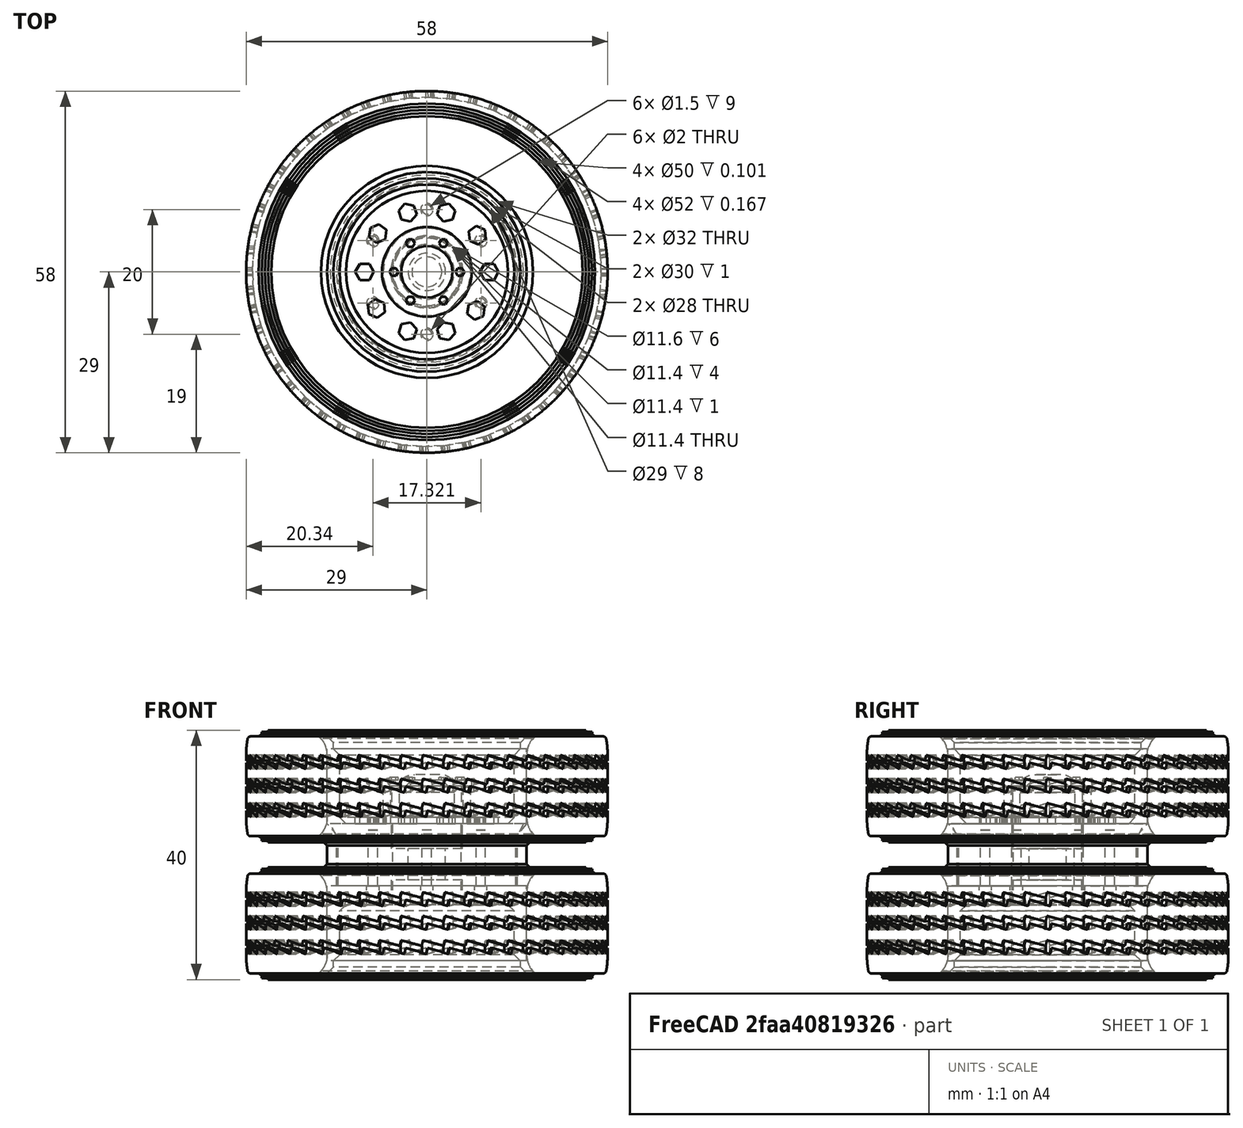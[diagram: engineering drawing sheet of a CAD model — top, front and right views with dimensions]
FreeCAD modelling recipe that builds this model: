
FCSTD DOCUMENT  (FreeCAD 0.18.4R)
Label: wheels
License: All rights reserved
LicenseURL: http://en.wikipedia.org/wiki/All_rights_reserved
objects: Part::Cylinder×44, Part::Cut×27, Part::MultiFuse×25, Part::Feature×24, Part::Fillet×10, Part::Chamfer×10, Part::RegularPolygon×4, Part::Extrusion×4, Part::Box×2, Part::Mirroring×2
note: 152 computed .brp shape members not serialized (recipe doc carries the construction recipe); baked Part::Feature solids carry a one-line shape summary decoded from their .brp

FEATURE [Part::Cylinder] Cylinder
  Angle = 360
  AttacherType = Attacher::AttachEngine3D
  Height = 18
  Radius = 29
FEATURE [Part::Cylinder] Cylinder001
  Angle = 360
  AttacherType = Attacher::AttachEngine3D
  Height = 18
  Radius = 16
FEATURE [Part::Cut] Cut
  Base = -> Cylinder
  Refine = true
  Tool = -> Cylinder001
FEATURE [Part::Fillet] Fillet
  Base = -> Cut
  Edges = 2 edges r=4: [Edge4,Edge5]
FEATURE [Part::Cylinder] Cylinder002
  Angle = 360
  AttacherType = Attacher::AttachEngine3D
  Height = 16
  Placement = pos=(0,0,1) rot=(0,0,1;0rad)
  Radius = 29
FEATURE [Part::Cylinder] Cylinder003
  Angle = 360
  AttacherType = Attacher::AttachEngine3D
  Height = 18
  Radius = 21
FEATURE [Part::Cut] Cut001
  Base = -> Cylinder002
  Refine = true
  Tool = -> Cylinder003
FEATURE [Part::Fillet] Fillet001
  Base = -> Fillet
  Edges = 2 edges r=5: [Edge2,Edge6]
FEATURE [Part::Box] Box  label="Cube"
  AttacherType = Attacher::AttachEngine3D
  Height = 2
  Length = 3
  Placement = pos=(27,0,4) rot=(0,0,1;0.05236rad)
  Width = 4
FEATURE [Part::Box] Box001  label="Cube001"
  AttacherType = Attacher::AttachEngine3D
  Height = 2
  Length = 2
  Placement = pos=(28,-1,5) rot=(0,0,1;0.05236rad)
  Width = 4
FEATURE [Part::Cut] Cut002
  Base = -> Box001
  Placement = pos=(0,-1,0) rot=(-1,0,0;0.261799rad)
  Refine = true
  Tool = -> Box
FEATURE [Part::Feature] Cut002001  label="Cut003"
  Placement = pos=(0,-1,0) rot=(-1,0,0;0.261799rad)
  shape: bbox 2.207 x 4.477 x 2.231 mm, 8 faces (baked)
FEATURE [Part::Mirroring] Part__Mirroring  label="Cut003 (Mirror #1)"
  Base = (0,0,0)
  Normal = (1,0,0)
  Source = -> Cut002001
FEATURE [Part::Mirroring] Part__Mirroring001  label="Cut003 (Mirror #2)"
  Base = (0,0,0)
  Normal = (0,1,0)
  Source = -> Part__Mirroring
FEATURE [Part::MultiFuse] Fusion001
  Refine = true
  Shapes = -> [Part__Mirroring001,Cut002]
FEATURE [Part::Feature] Fusion001001  label="Fusion002"
  Placement = pos=(0,0,0) rot=(0,0,1;3.01942rad)
  shape: bbox 60.06 x 8.444 x 2.231 mm, 16 faces, 2 solids (baked)
FEATURE [Part::Feature] Fusion001002  label="Fusion003"
  Placement = pos=(0,0,0) rot=(0,0,1;2.89725rad)
  shape: bbox 59.65 x 15.62 x 2.231 mm, 16 faces, 2 solids (baked)
FEATURE [Part::Feature] Fusion001003  label="Fusion004"
  Placement = pos=(0,0,0) rot=(0,0,1;2.77507rad)
  shape: bbox 58.35 x 22.57 x 2.231 mm, 16 faces, 2 solids (baked)
FEATURE [Part::Feature] Fusion001004  label="Fusion005"
  Placement = pos=(0,0,0) rot=(0,0,1;2.6529rad)
  shape: bbox 56.18 x 29.17 x 2.231 mm, 16 faces, 2 solids (baked)
FEATURE [Part::MultiFuse] Fusion001005
  Refine = true
  Shapes = -> [Fusion001001,Fusion001004,Fusion001002,Fusion001003]
FEATURE [Part::Feature] Fusion001005001  label="Fusion001006"
  Placement = pos=(0,0,0) rot=(0,0,-1;0.488692rad)
  shape: bbox 53.17 x 50.38 x 2.231 mm, 76 faces, 2 solids (baked)
FEATURE [Part::MultiFuse] Fusion001005002
  Refine = true
  Shapes = -> [Fusion001005001,Fusion001005]
FEATURE [Part::Feature] Fusion001005002001  label="Fusion001005003"
  Placement = pos=(0,0,0) rot=(0,0,-1;0.977384rad)
  shape: bbox 33.83 x 60.06 x 2.231 mm, 156 faces, 2 solids (baked)
FEATURE [Part::Feature] Fusion001005002002  label="Fusion001005004"
  Placement = pos=(0,0,0) rot=(0,0,-1;1.95477rad)
  shape: bbox 58.92 x 55.8 x 2.231 mm, 156 faces, 2 solids (baked)
FEATURE [Part::Feature] Fusion001005002003  label="Fusion001005005"
  Placement = pos=(0,0,0) rot=(0,0,1;0.10472rad)
  shape: bbox 59.79 x 13.8 x 2.231 mm, 16 faces, 2 solids (baked)
FEATURE [Part::MultiFuse] Fusion001005002004
  Placement = pos=(0,0,3.2) rot=(0,0,1;0rad)
  Refine = true
  Shapes = -> [Fusion001,Fusion001005002001,Fusion001005002003,Fusion001005002002,Fusion001005002]
FEATURE [Part::Feature] Fusion001005002004001  label="Fusion001005002005"
  Placement = pos=(0,0,7) rot=(0,0,1;0rad)
  shape: bbox 60.06 x 60.06 x 2.231 mm, 536 faces (baked)
FEATURE [Part::Feature] Fusion001005002004002  label="Fusion001005002006"
  Placement = pos=(0,0,-0.7) rot=(0,0,1;0rad)
  shape: bbox 60.06 x 60.06 x 2.231 mm, 536 faces (baked)
FEATURE [Part::MultiFuse] Fusion001005002004003
  Refine = true
  Shapes = -> [Fusion001005002004002,Fusion001005002004001,Fusion001005002004]
FEATURE [Part::Cylinder] Cylinder004
  Angle = 360
  AttacherType = Attacher::AttachEngine3D
  Height = 40
  Placement = pos=(0,0,-11) rot=(0,0,1;0rad)
  Radius = 29
FEATURE [Part::Fillet] Fillet002
  Base = -> Cylinder004
  Edges = 2 edges r=15: [Edge1,Edge3]
FEATURE [Part::Cylinder] Cylinder005
  Angle = 360
  AttacherType = Attacher::AttachEngine3D
  Height = 40
  Placement = pos=(0,0,-11) rot=(0,0,1;0rad)
  Radius = 30
FEATURE [Part::Cut] Cut002002
  Base = -> Cylinder005
  Refine = true
  Tool = -> Fillet002
FEATURE [Part::Cut] Cut002003
  Base = -> Cut001
  Refine = true
  Tool = -> Cut002002
FEATURE [Part::Fillet] Fillet003
  Base = -> Cut002003
  Edges = 2 edges r=0.5: [Edge5,Edge7]
FEATURE [Part::MultiFuse] Fusion
  Refine = true
  Shapes = -> [Fillet001,Fillet003]
FEATURE [Part::Cut] Cut002004
  Base = -> Fusion
  Refine = true
  Tool = -> Fusion001005002004003
FEATURE [Part::Cylinder] Cylinder006
  Angle = 360
  AttacherType = Attacher::AttachEngine3D
  Height = 17.5
  Placement = pos=(0,0,0.25) rot=(0,0,1;0rad)
  Radius = 26.5
FEATURE [Part::Cylinder] Cylinder007
  Angle = 360
  AttacherType = Attacher::AttachEngine3D
  Height = 17.5
  Placement = pos=(0,0,0.25) rot=(0,0,1;0rad)
  Radius = 26
FEATURE [Part::Cut] Cut002005
  Base = -> Cylinder006
  Refine = true
  Tool = -> Cylinder007
FEATURE [Part::Cylinder] Cylinder008
  Angle = 360
  AttacherType = Attacher::AttachEngine3D
  Height = 18
  Radius = 25.5
FEATURE [Part::Cylinder] Cylinder009
  Angle = 360
  AttacherType = Attacher::AttachEngine3D
  Height = 18
  Radius = 25
FEATURE [Part::Cut] Cut002006
  Base = -> Cylinder008
  Refine = true
  Tool = -> Cylinder009
FEATURE [Part::MultiFuse] Fusion001005002004004  label="tire-inner"
  Refine = true
  Shapes = -> [Cut002004,Cut002005,Cut002006]
FEATURE [Part::Cylinder] Cylinder719
  Angle = 360
  AttacherType = Attacher::AttachEngine3D
  Height = 14
  Radius = 16
FEATURE [Part::Cylinder] Cylinder720
  Angle = 360
  AttacherType = Attacher::AttachEngine3D
  Height = 2
  Radius = 17
FEATURE [Part::MultiFuse] Fusion088026026
  Placement = pos=(0,0,1) rot=(0,0,1;0rad)
  Refine = true
  Shapes = -> [Cylinder719,Cylinder720]
FEATURE [Part::Cylinder] Cylinder793
  Angle = 360
  AttacherType = Attacher::AttachEngine3D
  Height = 18
  Radius = 29
FEATURE [Part::Cylinder] Cylinder794
  Angle = 360
  AttacherType = Attacher::AttachEngine3D
  Height = 18
  Radius = 16
FEATURE [Part::Cut] Cut176013009049
  Base = -> Cylinder793
  Refine = true
  Tool = -> Cylinder794
FEATURE [Part::Fillet] Fillet567
  Base = -> Cut176013009049
  Edges = 2 edges r=4: [Edge4,Edge5]
FEATURE [Part::Fillet] Fillet566
  Base = -> Fillet567
  Edges = 2 edges r=5: [Edge2,Edge6]
FEATURE [Part::Cut] Cut176013009050
  Base = -> Fusion088026026
  Refine = true
  Tool = -> Fillet566
FEATURE [Part::Feature] Fusion001005002004004001  label="tire-outer"
  Placement = pos=(0,0,22) rot=(0,0,1;0rad)
  shape: bbox 59.64 x 59.64 x 18 mm, 1212 faces (baked)
FEATURE [Part::Cylinder] Cylinder795
  Angle = 360
  AttacherType = Attacher::AttachEngine3D
  Height = 2
  Placement = pos=(0,0,37) rot=(-1,0,0;0rad)
  Radius = 17
FEATURE [Part::Cylinder] Cylinder796
  Angle = 360
  AttacherType = Attacher::AttachEngine3D
  Height = 24
  Placement = pos=(0,0,15) rot=(-1,0,0;0rad)
  Radius = 16
FEATURE [Part::MultiFuse] Fusion001005002004004002
  Refine = true
  Shapes = -> [Cylinder796,Cylinder795]
FEATURE [Part::Cylinder] Cylinder797
  Angle = 360
  AttacherType = Attacher::AttachEngine3D
  Height = 18
  Radius = 16
FEATURE [Part::Cylinder] Cylinder798
  Angle = 360
  AttacherType = Attacher::AttachEngine3D
  Height = 18
  Radius = 29
FEATURE [Part::Cut] Cut176013009051
  Base = -> Cylinder798
  Refine = true
  Tool = -> Cylinder797
FEATURE [Part::Fillet] Fillet569
  Base = -> Cut176013009051
  Edges = 2 edges r=4: [Edge4,Edge5]
FEATURE [Part::Fillet] Fillet568
  Base = -> Fillet569
  Edges = 2 edges r=5: [Edge2,Edge6]
  Placement = pos=(0,0,22) rot=(0,0,1;0rad)
FEATURE [Part::Cut] Cut176013009052
  Base = -> Fusion001005002004004002
  Refine = true
  Tool = -> Fillet568
FEATURE [Part::Cylinder] Cylinder799
  Angle = 360
  AttacherType = Attacher::AttachEngine3D
  Height = 10
  Placement = pos=(0,0,15) rot=(-1,0,0;0rad)
  Radius = 17
FEATURE [Part::Feature] Fillet568001  label="Fillet570"
  Placement = pos=(0,0,22) rot=(0,0,1;0rad)
  shape: bbox 62.78 x 62.78 x 18 mm, 8 faces (baked)
FEATURE [Part::Feature] Fillet566001  label="Fillet571"
  shape: bbox 62.78 x 62.78 x 18 mm, 8 faces (baked)
FEATURE [Part::MultiFuse] Fusion001005002004004003
  Refine = true
  Shapes = -> [Fillet568001,Fillet566001]
FEATURE [Part::Cut] Cut176013009053
  Base = -> Cylinder799
  Refine = true
  Tool = -> Fusion001005002004004003
FEATURE [Part::Cylinder] Cylinder800
  Angle = 360
  AttacherType = Attacher::AttachEngine3D
  Height = 10
  Radius = 14.25
FEATURE [Part::Cylinder] Cylinder801
  Angle = 360
  AttacherType = Attacher::AttachEngine3D
  Height = 10
  Radius = 16
FEATURE [Part::Cut] Cut176013009054
  Base = -> Cylinder801
  Placement = pos=(0,0,15) rot=(0,0,1;0rad)
  Refine = true
  Tool = -> Cylinder800
FEATURE [Part::Cylinder] Cylinder802
  Angle = 360
  AttacherType = Attacher::AttachEngine3D
  Height = 10
  Placement = pos=(0,0,15) rot=(-1,0,0;0rad)
  Radius = 14.5
FEATURE [Part::Cut] Cut176013009055
  Base = -> Cut176013009053
  Refine = true
  Tool = -> Cylinder802
FEATURE [Part::Cylinder] Cylinder803
  Angle = 360
  AttacherType = Attacher::AttachEngine3D
  Height = 5
  Placement = pos=(0,0,17.5) rot=(-1,0,0;0rad)
  Radius = 17
FEATURE [Part::Cylinder] Cylinder804
  Angle = 360
  AttacherType = Attacher::AttachEngine3D
  Height = 5
  Placement = pos=(0,0,17.5) rot=(-1,0,0;0rad)
  Radius = 16
FEATURE [Part::Cut] Cut176013009058
  Base = -> Cylinder803
  Refine = true
  Tool = -> Cylinder804
FEATURE [Part::Chamfer] Chamfer017002
  Base = -> Cut176013009058
  Edges = 2 edges r=0.999: [Edge4,Edge5]
FEATURE [Part::Cylinder] Cylinder805
  Angle = 360
  AttacherType = Attacher::AttachEngine3D
  Height = 12
  Radius = 14
FEATURE [Part::Cut] Cut176013009060
  Base = -> Cut176013009050
  Refine = true
  Tool = -> Cylinder805
FEATURE [Part::Cylinder] Cylinder806
  Angle = 360
  AttacherType = Attacher::AttachEngine3D
  Height = 3
  Radius = 15
FEATURE [Part::Cut] Cut176013009061
  Base = -> Cut176013009060
  Refine = true
  Tool = -> Cylinder806
FEATURE [Part::Chamfer] Chamfer017003
  Base = -> Cut176013009061
  Edges = 1 edges r=1: [Edge9]
FEATURE [Part::Chamfer] Chamfer017004
  Base = -> Chamfer017003
  Edges = 1 edges r=0.999: [Edge11]
FEATURE [Part::Chamfer] Chamfer017005
  Base = -> Chamfer017004
  Edges = 1 edges r=1: [Edge8]
FEATURE [Part::Chamfer] Chamfer017006
  Base = -> Cut176013009054
  Edges = 1 edges: [Edge4 r1=1.749 r2=2]
FEATURE [Part::Cut] Cut176013009062
  Base = -> Cut176013009052
  Refine = true
  Tool = -> Chamfer017006
FEATURE [Part::Chamfer] Chamfer017007
  Base = -> Cut176013009055
  Edges = 1 edges: [Edge8 r1=1 r2=2]
FEATURE [Part::Cut] Cut176013009063  label="rim-central"
  Base = -> Chamfer017007
  Refine = true
  Tool = -> Chamfer017002
FEATURE [Part::Cylinder] Cylinder807
  Angle = 360
  AttacherType = Attacher::AttachEngine3D
  Height = 15
  Placement = pos=(0,0,25) rot=(-1,0,0;0rad)
  Radius = 14
FEATURE [Part::Cylinder] Cylinder808
  Angle = 360
  AttacherType = Attacher::AttachEngine3D
  Height = 3
  Placement = pos=(0,0,37) rot=(-1,0,0;0rad)
  Radius = 15
FEATURE [Part::MultiFuse] Fusion001005002004004004
  Refine = true
  Shapes = -> [Cylinder807,Cylinder808]
FEATURE [Part::Cut] Cut176013009064
  Base = -> Cut176013009062
  Refine = true
  Tool = -> Fusion001005002004004004
FEATURE [Part::Chamfer] Chamfer017008
  Base = -> Cut176013009064
  Edges = 2 edges r=1: [Edge14,Edge19]
FEATURE [Part::Chamfer] Chamfer017009
  Base = -> Chamfer017008
  Edges = 1 edges r=0.999: [Edge11]
FEATURE [Part::Cylinder] Cylinder809
  Angle = 360
  AttacherType = Attacher::AttachEngine3D
  Height = 40
  Radius = 3
FEATURE [Part::Cylinder] Cylinder810
  Angle = 360
  AttacherType = Attacher::AttachEngine3D
  Height = 4
  Placement = pos=(0,0,21) rot=(-1,0,0;0rad)
  Radius = 5.7
FEATURE [Part::Cylinder] Cylinder811
  Angle = 360
  AttacherType = Attacher::AttachEngine3D
  Height = 4
  Placement = pos=(0,0,12) rot=(-1,0,0;0rad)
  Radius = 5.7
FEATURE [Part::MultiFuse] Fusion001005002004004005
  Refine = true
  Shapes = -> [Cylinder809,Cylinder810,Cylinder811]
FEATURE [Part::Cut] Cut176013009065
  Base = -> Chamfer017005
  Refine = true
  Tool = -> Fusion001005002004004005
FEATURE [Part::RegularPolygon] RegularPolygon  label="Regular polygon"
  AttacherType = Attacher::AttachEngine3D
  Circumradius = 1.5
  Placement = pos=(-10,0,0) rot=(0,0,1;0rad)
  Polygon = 6
FEATURE [Part::Extrusion] Extrude
  Base = -> RegularPolygon
  Dir = (0,0,1)
  DirMode = 0
  FaceMakerClass = Part::FaceMakerBullseye
  LengthFwd = 1
  LengthRev = 0
  Placement = pos=(0,0,11) rot=(0,0,1;0rad)
  Solid = true
  Symmetric = false
FEATURE [Part::RegularPolygon] RegularPolygon001  label="Regular polygon001"
  AttacherType = Attacher::AttachEngine3D
  Circumradius = 1.5
  Placement = pos=(-10,0,0) rot=(0,0,1;0rad)
  Polygon = 6
FEATURE [Part::Extrusion] Extrude001
  Base = -> RegularPolygon001
  Dir = (0,0,1)
  DirMode = 0
  FaceMakerClass = Part::FaceMakerBullseye
  LengthFwd = 1
  LengthRev = 0
  Placement = pos=(20,0,11) rot=(0,0,1;0rad)
  Solid = true
  Symmetric = false
FEATURE [Part::MultiFuse] Fusion001005002004004005002
  Refine = true
  Shapes = -> [Extrude001,Extrude]
FEATURE [Part::Feature] Fusion001005002004004005002001  label="Fusion001005002004004005003"
  Placement = pos=(0,0,0) rot=(0,0,1;0.628319rad)
  shape: bbox 18.92 x 14.74 x 1 mm, 16 faces, 2 solids (baked)
FEATURE [Part::Feature] Fusion001005002004004005002002  label="Fusion001005002004004005004"
  Placement = pos=(0,0,0) rot=(0,0,1;1.25664rad)
  shape: bbox 9.115 x 21.87 x 1 mm, 16 faces, 2 solids (baked)
FEATURE [Part::Feature] Fusion001005002004004005002003  label="Fusion001005002004004005005"
  Placement = pos=(0,0,0) rot=(0,0,1;1.88496rad)
  shape: bbox 9.115 x 21.87 x 1 mm, 16 faces, 2 solids (baked)
FEATURE [Part::Feature] Fusion001005002004004005002004  label="Fusion001005002004004005006"
  Placement = pos=(0,0,0) rot=(0,0,1;2.47837rad)
  shape: bbox 18.54 x 15.28 x 1 mm, 16 faces, 2 solids (baked)
FEATURE [Part::MultiFuse] Fusion001005002004004005002005
  Placement = pos=(0,0,14) rot=(0,0,1;0rad)
  Refine = true
  Shapes = -> [Fusion001005002004004005002,Fusion001005002004004005002001,Fusion001005002004004005002002,Fusion001005002004004005002004,Fusion001005002004004005002003]
FEATURE [Part::Cylinder] Cylinder812
  Angle = 360
  AttacherType = Attacher::AttachEngine3D
  Height = 6
  Placement = pos=(0,0,25) rot=(-1,0,0;0rad)
  Radius = 7
FEATURE [Part::Cylinder] Cylinder813
  Angle = 360
  AttacherType = Attacher::AttachEngine3D
  Height = 6
  Placement = pos=(0,0,25) rot=(-1,0,0;0rad)
  Radius = 5.8
FEATURE [Part::Cut] Cut176013009067
  Base = -> Cylinder812
  Refine = true
  Tool = -> Cylinder813
FEATURE [Part::Feature] Fusion058011001  label="Fusion058012"
  Placement = pos=(0,0,0) rot=(0,0,1;1.0472rad)
  shape: bbox 6.7 x 10.39 x 0.5 mm, 16 faces, 2 solids (baked)
FEATURE [Part::Cylinder] Cylinder100
  Angle = 360
  AttacherType = Attacher::AttachEngine3D
  Height = 5
  Placement = pos=(0,0,11) rot=(0,0,1;0rad)
  Radius = 6
FEATURE [Part::Cylinder] Cylinder098
  Angle = 360
  AttacherType = Attacher::AttachEngine3D
  Height = 11
  Placement = pos=(0,0,12) rot=(0,0,1;0rad)
  Radius = 4.4
FEATURE [Part::Cylinder] Cylinder099
  Angle = 360
  AttacherType = Attacher::AttachEngine3D
  Height = 1
  Placement = pos=(0,0,20) rot=(0,0,1;0rad)
  Radius = 7.2
FEATURE [Part::Feature] Fusion058011002  label="Fusion058013"
  Placement = pos=(0,0,0) rot=(0,0,1;2.0944rad)
  shape: bbox 6.7 x 10.39 x 0.5 mm, 16 faces, 2 solids (baked)
FEATURE [Part::Fillet] Fillet059
  Base = -> Cylinder099
  Edges = 1 edges r=0.5: [Edge1]
  Placement = pos=(0,0,11) rot=(0,0,1;0rad)
FEATURE [Part::RegularPolygon] RegularPolygon003  label="Regular polygon003"
  AttacherType = Attacher::AttachEngine3D
  Circumradius = 0.7
  Polygon = 6
FEATURE [Part::Extrusion] Extrude010003
  Base = -> RegularPolygon003
  Dir = (0,0,1)
  DirMode = 0
  FaceMakerClass = Part::FaceMakerBullseye
  LengthFwd = 0.5
  LengthRev = 0
  Placement = pos=(-5.3,0,21.9) rot=(0,0,1;0rad)
  Solid = true
  Symmetric = false
FEATURE [Part::Cylinder] Cylinder101
  Angle = 360
  AttacherType = Attacher::AttachEngine3D
  Height = 3.8
  Placement = pos=(0,0,19.4) rot=(0,0,1;0rad)
  Radius = 5
FEATURE [Part::Fillet] Fillet006004006
  Base = -> Cylinder101
  Edges = 1 edges r=3: [Edge1]
  Placement = pos=(0,0,9.7) rot=(0,0,1;0rad)
FEATURE [Part::MultiFuse] Fusion041
  Refine = true
  Shapes = -> [Cylinder098,Cylinder100]
FEATURE [Part::Chamfer] Chamfer001
  Base = -> Fusion041
  Edges = 1 edges r=2: [Edge1]
  Placement = pos=(0,0,9) rot=(0,0,1;0rad)
FEATURE [Part::Cylinder] Cylinder097
  Angle = 360
  AttacherType = Attacher::AttachEngine3D
  Height = 6
  Placement = pos=(0,0,26) rot=(0,0,1;0rad)
  Radius = 5.55
FEATURE [Part::RegularPolygon] RegularPolygon002  label="Regular polygon002"
  AttacherType = Attacher::AttachEngine3D
  Circumradius = 0.7
  Polygon = 6
FEATURE [Part::Extrusion] Extrude010002
  Base = -> RegularPolygon002
  Dir = (0,0,1)
  DirMode = 0
  FaceMakerClass = Part::FaceMakerBullseye
  LengthFwd = 0.5
  LengthRev = 0
  Placement = pos=(5.3,0,21.9) rot=(0,0,1;0rad)
  Solid = true
  Symmetric = false
FEATURE [Part::MultiFuse] Fusion058011
  Refine = true
  Shapes = -> [Extrude010003,Extrude010002]
FEATURE [Part::MultiFuse] Fusion058011003
  Placement = pos=(0,0,10) rot=(0,0,1;0rad)
  Refine = true
  Shapes = -> [Fusion058011002,Fusion058011,Fusion058011001]
FEATURE [Part::MultiFuse] Fusion001005002004004005002007
  Refine = true
  Shapes = -> [Fillet006004006,Fillet059,Cylinder097]
FEATURE [Part::Cut] Cut176013009068
  Base = -> Fusion001005002004004005002007
  Refine = true
  Tool = -> Chamfer001
FEATURE [Part::MultiFuse] Fusion001005002004004005002008  label="Fusion-0000"
  Refine = true
  Shapes = -> [Fusion058011003,Cut176013009068]
FEATURE [Part::Cylinder] Cylinder814
  Angle = 360
  AttacherType = Attacher::AttachEngine3D
  Height = 3
  Placement = pos=(0,10,12) rot=(0,0,1;0rad)
  Radius = 1
FEATURE [Part::Cylinder] Cylinder815
  Angle = 360
  AttacherType = Attacher::AttachEngine3D
  Height = 12
  Placement = pos=(0,10,12) rot=(0,0,1;0rad)
  Radius = 0.75
FEATURE [Part::MultiFuse] Fusion001005002004004005002010
  Refine = true
  Shapes = -> [Cylinder814,Cylinder815]
FEATURE [Part::Feature] Fusion001005002004004005002010001  label="Fusion001005002004004005002011"
  Placement = pos=(0,-20,0) rot=(0,0,1;0rad)
  shape: bbox 2 x 2 x 12 mm, 5 faces (baked)
FEATURE [Part::MultiFuse] Fusion001005002004004005002010002
  Refine = true
  Shapes = -> [Fusion001005002004004005002010001,Fusion001005002004004005002010]
FEATURE [Part::Feature] Fusion001005002004004005002010002001  label="Fusion001005002004004005002010003"
  Placement = pos=(0,0,0) rot=(0,0,1;2.0944rad)
  shape: bbox 19.32 x 12 x 12 mm, 10 faces, 2 solids (baked)
FEATURE [Part::Feature] Fusion001005002004004005002010002002  label="Fusion001005002004004005002010004"
  Placement = pos=(0,0,0) rot=(0,0,1;4.18879rad)
  shape: bbox 19.32 x 12 x 12 mm, 10 faces, 2 solids (baked)
FEATURE [Part::MultiFuse] Fusion001005002004004005002010002003
  Refine = true
  Shapes = -> [Fusion001005002004004005002010002002,Fusion001005002004004005002010002001,Fusion001005002004004005002010002]
FEATURE [Part::Feature] Fusion001005002004004005002010002003001  label="Fusion001005002004004005002010002004"
  shape: bbox 19.32 x 22 x 12 mm, 30 faces, 6 solids (baked)
FEATURE [Part::Cut] Cut176013009069  label="rim-inner"
  Base = -> Cut176013009065
  Refine = true
  Tool = -> Fusion001005002004004005002010002003
FEATURE [Part::Cylinder] Cylinder816
  Angle = 360
  AttacherType = Attacher::AttachEngine3D
  Height = 40
  Radius = 3
FEATURE [Part::Cylinder] Cylinder817
  Angle = 360
  AttacherType = Attacher::AttachEngine3D
  Height = 4
  Placement = pos=(0,0,21) rot=(-1,0,0;0rad)
  Radius = 5.7
FEATURE [Part::Cylinder] Cylinder818
  Angle = 360
  AttacherType = Attacher::AttachEngine3D
  Height = 4
  Placement = pos=(0,0,12) rot=(-1,0,0;0rad)
  Radius = 5.7
FEATURE [Part::MultiFuse] Fusion001005002004004005002010002003002
  Refine = true
  Shapes = -> [Cylinder816,Cylinder817,Cylinder818]
FEATURE [Part::Cut] Cut176013009070
  Base = -> Chamfer017009
  Refine = true
  Tool = -> Fusion001005002004004005002010002003002
FEATURE [Part::MultiFuse] Fusion001005002004004005002010002003003
  Refine = true
  Shapes = -> [Cut176013009070,Fusion001005002004004005002005]
FEATURE [Part::MultiFuse] Fusion001005002004004005002010002003004
  Refine = true
  Shapes = -> [Cut176013009067,Fusion001005002004004005002010002003003]
FEATURE [Part::Cut] Cut176013009071  label="rim-outer"
  Base = -> Fusion001005002004004005002010002003004
  Refine = true
  Tool = -> Fusion001005002004004005002010002003001
FEATURE [Part::Cylinder] Cylinder819
  Angle = 360
  AttacherType = Attacher::AttachEngine3D
  Height = 13
  Placement = pos=(0,0,12) rot=(-1,0,0;0rad)
  Radius = 5.5
FEATURE [Part::Chamfer] Chamfer  label="rim-cap"
  Base = -> Fusion001005002004004005002008
  Edges = 1 edges r=0.2: [Edge119]
